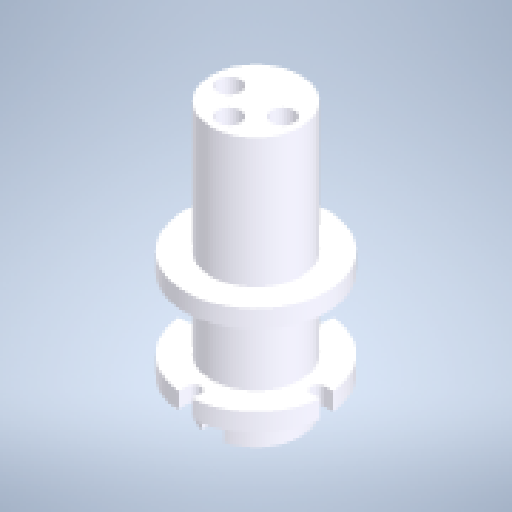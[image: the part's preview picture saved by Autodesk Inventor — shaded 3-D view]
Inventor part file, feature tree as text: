
AUTODESK INVENTOR PART (.ipt)
format: ipt  version: 2023 (Build 270158000, 158)  size: 383,488 bytes
history: native  units: mm
features: sketch x5, extrude x3, hole x2, revolve x1, pattern_circular x1
ambient origin geometry x8: Origin, YZ Plane, XZ Plane, XY Plane, X Axis, Y Axis, Z Axis, Center Point
bodies: Body1 (feature_tree)
feature tree (12):
  revolve  "Revolution1"  [1 undecoded]
  hole  "Hole2"  [1 undecoded]
  extrude  "Extrusion5"  Depth=20.0mm
  pattern_circular  "Circular Pattern1"  [2 undecoded]
  extrude  "Extrusion6"  Depth=1.5mm
  hole  "Hole3"  [1 undecoded]
  extrude  "Extrusion7"  Depth=8.0mm TaperAngle=0.0deg
  sketch  "Sketch6"  dims[d17=31.7mm d18=7.0mm]
  sketch  "Sketch8"  dims[d19=4.0mm d23=20.0mm]
  sketch  "Sketch9"  dims[d26=60.0mm d27=20.0mm]
  sketch  "Sketch10"  dims[d28=90.0deg]
  sketch  "Sketch11"  dims[d29=12.0mm d30=3.0mm d31=6.0mm d32=5.0mm d33=15.0mm d34=90.0deg d35=8.0mm d36=20.594885mm d40=13.88mm d41=1.5mm d42=4.0mm d43=8.0mm d44=0.0mm d45=40.0mm d46=360.0deg d48=31.7mm d49=16.0mm d50=4.0mm d51=5.0mm d53=5.0mm d54=15.0mm d55=0.0mm d56=8.0mm d57=6.0mm d58=3.0mm d59=6.0mm d60=5.0mm d61=15.0mm d62=90.0deg d63=10.0mm d64=20.594885mm d65=11.0mm d66=7.5mm d67=0.0mm d68=5.0mm]
note: 5 required parameter values undecoded (feature->parameter linkage not recoverable at this tier; creation-order binding heuristic only, values carry confidence <= 0.55)